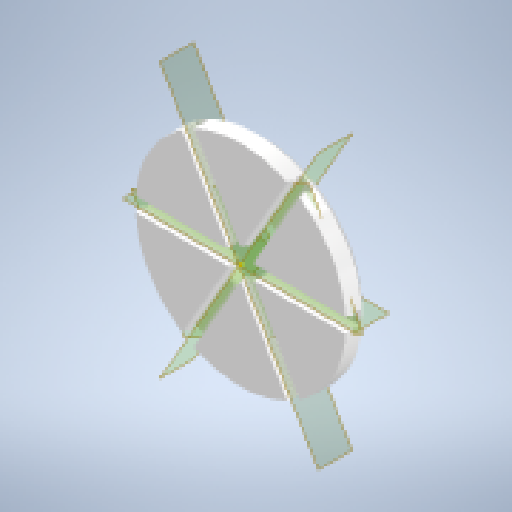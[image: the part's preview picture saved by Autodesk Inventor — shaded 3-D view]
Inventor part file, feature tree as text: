
AUTODESK INVENTOR PART (.ipt)
format: ipt  version: 2024 (Build 280153000, 153)  size: 781,312 bytes
history: native  units: mm
features: extrude x7, plane x6, chamfer x5, sketch x4, fillet x3, pattern_circular x2, projected_geometry x1
ambient origin geometry x8: Origin, YZ Plane, XZ Plane, XY Plane, X Axis, Y Axis, Z Axis, Center Point
bodies: Solid1 (feature_tree)
feature tree (28):
  sketch  "Sketch1"  dims[d0=180.0mm d1=78.2mm]
  extrude  "Extrusion1"  Depth=78.2mm
  extrude  "Extrusion2"  Depth=26.0mm
  plane  "Work Plane2"
  extrude  "Extrusion3"  Depth=12.0mm TaperAngle=0.0deg
  extrude  "Extrusion4"  Depth=1.0mm
  chamfer  "Chamfer1"  Distance=4.0mm
  chamfer  "Chamfer2"  Distance=8.0mm
  chamfer  "Chamfer3"  Distance=6.25mm Angle=45.0deg
  chamfer  "Chamfer4"  Distance=6.0mm Angle=45.0deg
  extrude  "Extrusion5"  Depth=1.0mm TaperAngle=45.0deg
  chamfer  "Chamfer5"  Distance=4.0mm Angle=45.0deg
  pattern_circular  "Circular Pattern1"  [2 undecoded]
  fillet  "Fillet1"  Radius=3.0mm
  fillet  "Fillet2"  Radius=2.0mm
  plane  "Work Plane3"
  plane  "Work Plane4"
  plane  "Work Plane5"
  plane  "Work Plane6"
  sketch  "Sketch3"  dims[d4=2.0mm d5=12.0mm d6=0.0mm]
  sketch  "Sketch4"  dims[d7=4.0mm d8=0.0mm d9=10.25mm d10=4.0mm d11=0.0mm d12=8.0mm d13=0.0mm d14=6.25mm d15=2.0mm d16=45.0deg d17=6.0mm d18=2.0mm d19=45.0deg d20=1.0mm d21=2.0mm d22=45.0deg d23=4.0mm d24=2.0mm d25=45.0deg d26=8.0mm d28=3.0mm d29=2.0mm d30=0.0mm d31=0.0mm d32=2.0mm d33=2.0mm d34=45.0deg d35=0.5mm d36=1.0mm d37=60.0mm d38=360.0deg d40=4.0mm d41=15.0mm d42=20.0mm d43=6.0mm d44=0.0mm d45=45.0deg d46=30.0deg d47=6.0mm d48=0.0mm d49=1.0mm d50=60.0mm d51=360.0deg]
  extrude  "Extrusion6"  TaperAngle=0.0deg  [1 undecoded]
  plane  "Work Plane7"
  extrude  "Extrusion7"  Depth=1.0mm TaperAngle=45.0deg
  fillet  "Fillet3"  Radius=0.5mm
  pattern_circular  "Circular Pattern2"  [2 undecoded]
  sketch  "Sketch2"  dims[d2=90.0mm d3=26.0mm]
  projected_geometry  "Project Cut Edges1"
note: 5 required parameter values undecoded (feature->parameter linkage not recoverable at this tier; creation-order binding heuristic only, values carry confidence <= 0.55)
